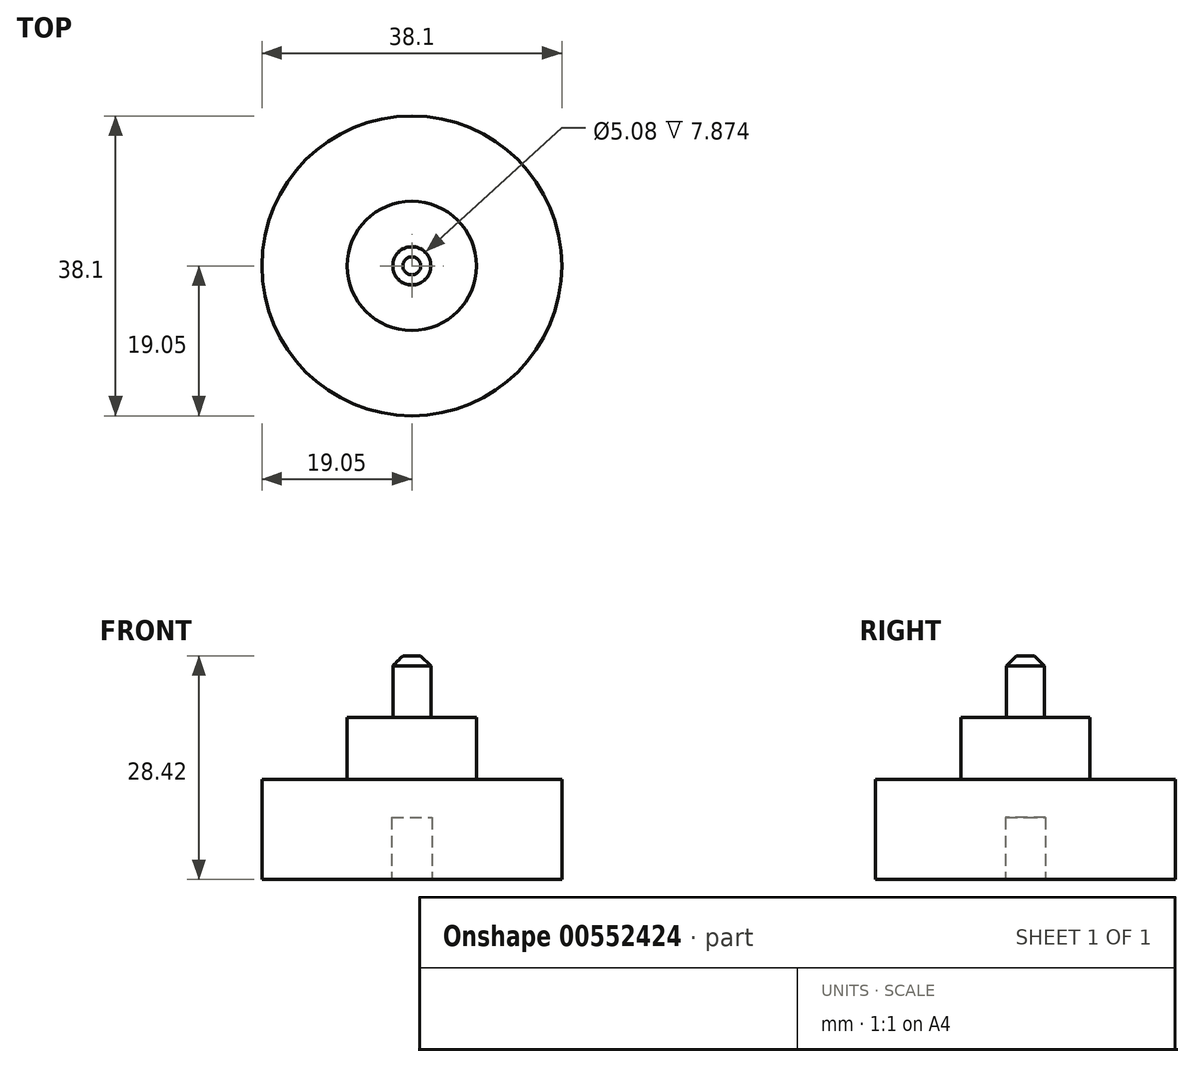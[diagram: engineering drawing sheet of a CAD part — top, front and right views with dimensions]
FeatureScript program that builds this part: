
annotation { "Feature Type Name" : "Feature", "Feature Type Description" : "" }
export const myFeature = defineFeature(function(context is Context, id is Id, definition is map)
    precondition{}
    {
        {
            var Q0;
            Q0=qCreatedBy(makeId("Front.planeOp"),FACE);
            var sketch = newSketch(context, id + "F0", { "sketchPlane" : qUnion([Q0])});
            skLineSegment(sketch, "E0", {"start": v(19.05, 0) * mm, "end": v(19.05, 12.7) * mm});
            skLineSegment(sketch, "E1", {"start": v(19.05, 12.7) * mm, "end": v(8.2, 12.7) * mm});
            skLineSegment(sketch, "E2", {"start": v(2.41, 20.57) * mm, "end": v(8.2, 20.57) * mm});
            skLineSegment(sketch, "E3", {"start": v(8.2, 20.57) * mm, "end": v(8.2, 12.7) * mm});
            skLineSegment(sketch, "E4", {"start": v(0, 28.42) * mm, "end": v(2.41, 28.42) * mm});
            skLineSegment(sketch, "E5", {"start": v(2.41, 28.42) * mm, "end": v(2.41, 20.57) * mm});
            skPoint(sketch, "E6.start.orphan", {"position": v(0, 12.7) * mm});
            skPoint(sketch, "E7.start.orphan", {"position": v(0, 20.57) * mm});
            skLineSegment(sketch, "E8", {"start": v(0, 7.87) * mm, "end": v(0, 28.42) * mm});
            skLineSegment(sketch, "E9", {"start": v(2.54, 0) * mm, "end": v(2.54, 7.87) * mm});
            skLineSegment(sketch, "E10", {"start": v(2.54, 7.87) * mm, "end": v(0, 7.87) * mm});
            skPoint(sketch, "E11.start.orphan", {"position": v(0, 0) * mm});
            skLineSegment(sketch, "E12", {"start": v(2.54, 0) * mm, "end": v(19.05, 0) * mm});
            skSolve(sketch);
        }
        {
            var Q0;
            Q0 = qSketchRegion(id + "F0", true);
            var Q1;
            Q1=sQuery(id+"F0.wireOp",EDGE,"E8");
            revolve(context, id + "F1", {"entities" : qUnion([Q0]), "axis" : qUnion([Q1]), "revolveType" : RevolveType.FULL});
        }
        {
            var Q0;
            Q0=makeQuery(id+"F1.opRevolve","SWEPT_EDGE",EDGE,{"disambiguationData":[OSD([sQuery(id+"F0.wireOp",EDGE,"E4"),sQuery(id+"F0.wireOp",EDGE,"E5")])]});
            chamfer(context, id + "F2", {"entities" : qUnion([Q0]), "width" : 1.27 * mm, "tangentPropagation" : true});
        }
    });
